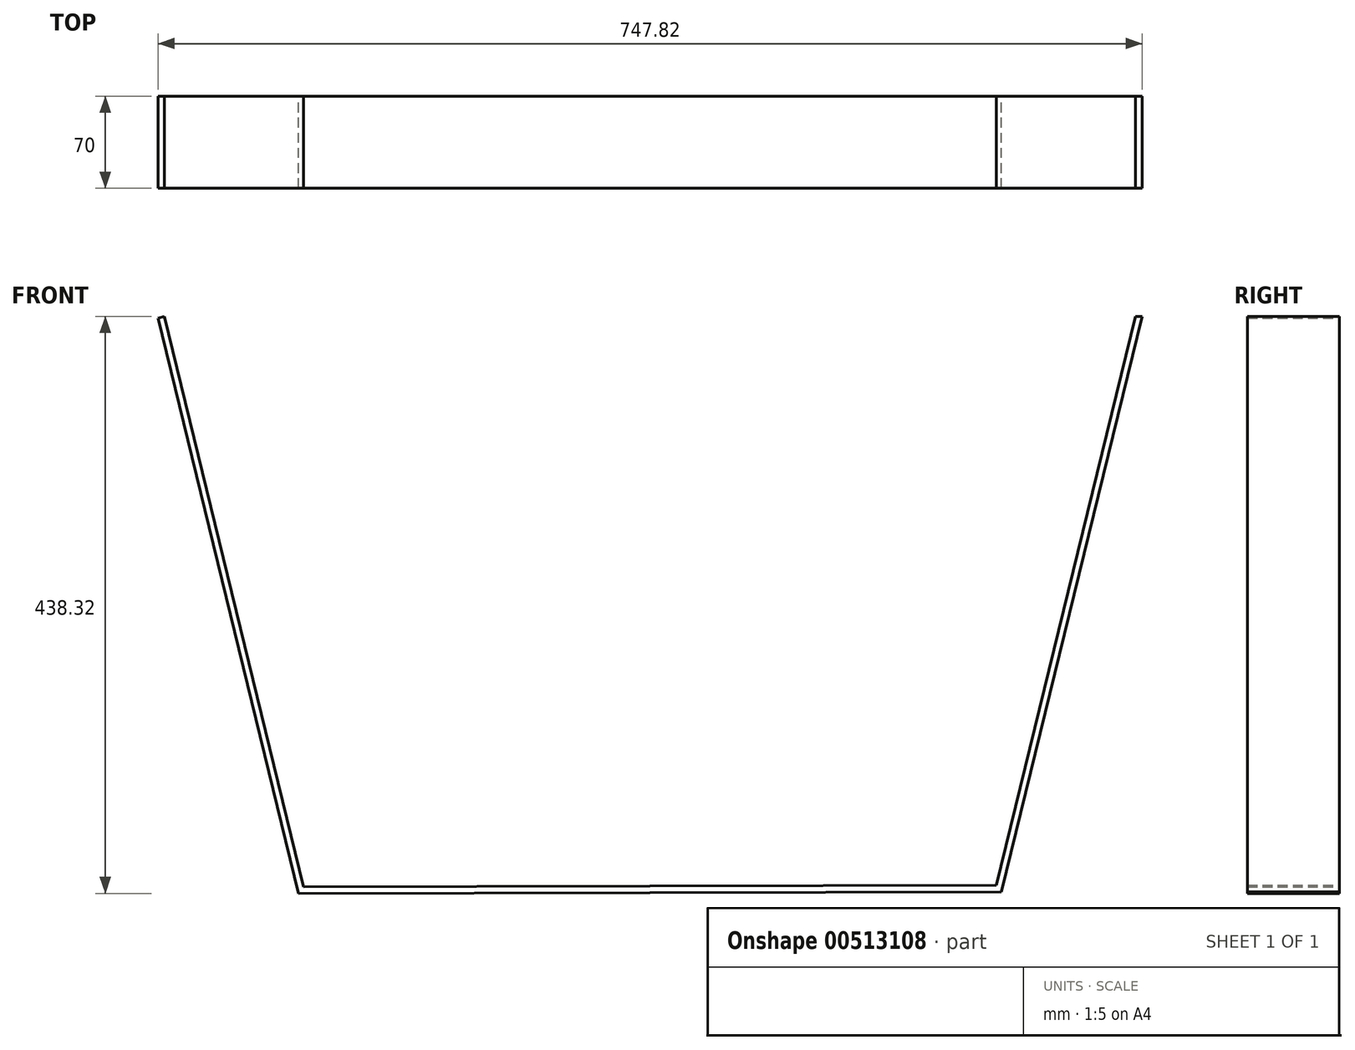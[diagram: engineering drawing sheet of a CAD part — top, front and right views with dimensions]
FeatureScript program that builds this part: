
annotation { "Feature Type Name" : "Feature", "Feature Type Description" : "" }
export const myFeature = defineFeature(function(context is Context, id is Id, definition is map)
    precondition{}
    {
        {
            var Q0;
            Q0=qCreatedBy(makeId("Front.planeOp"),FACE);
            var sketch = newSketch(context, id + "F0", { "sketchPlane" : qUnion([Q0])});
            skLineSegment(sketch, "E0.1", {"start": v(-436.34, 213.95) * mm, "end": v(-436.34, -176.05) * mm});
            skLineSegment(sketch, "E0.3", {"start": v(103.66, 213.95) * mm, "end": v(103.66, -176.05) * mm});
            skLineSegment(sketch, "E1", {"start": v(-465.58, -206.05) * mm, "end": v(133.66, -206.05) * mm});
            skLineSegment(sketch, "E2", {"start": v(-436.34, -176.05) * mm, "end": v(103.66, -176.05) * mm});
            skLineSegment(sketch, "E3", {"start": v(-436.34, 213.95) * mm, "end": v(103.66, 213.95) * mm});
            skLineSegment(sketch, "E4", {"start": v(-465.58, 243.95) * mm, "end": v(133.66, 243.95) * mm});
            skLineSegment(sketch, "E5", {"start": v(-465.58, 243.95) * mm, "end": v(-575.58, 243.95) * mm});
            skLineSegment(sketch, "E6", {"start": v(133.66, 243.95) * mm, "end": v(243.66, 243.95) * mm});
            skLineSegment(sketch, "E7", {"start": v(-575.58, 243.95) * mm, "end": v(-465.58, -206.05) * mm});
            skLineSegment(sketch, "E8", {"start": v(243.66, 243.95) * mm, "end": v(133.66, -206.05) * mm});
            skLineSegment(sketch, "E9.0", {"start": v(-537.36, 213.95) * mm, "end": v(-495.58, 43.02) * mm});
            skLineSegment(sketch, "E9.1", {"start": v(-495.58, 213.95) * mm, "end": v(-537.36, 213.95) * mm});
            skLineSegment(sketch, "E9.2", {"start": v(-495.58, 213.95) * mm, "end": v(-495.58, 43.02) * mm});
            skLineSegment(sketch, "E10.0", {"start": v(205.44, 213.95) * mm, "end": v(163.66, 43.02) * mm});
            skLineSegment(sketch, "E10.1", {"start": v(163.66, 213.95) * mm, "end": v(205.44, 213.95) * mm});
            skLineSegment(sketch, "E10.2", {"start": v(163.66, 213.95) * mm, "end": v(163.66, 43.02) * mm});
            skSolve(sketch);
        }
        {
            var Q0;
            Q0=makeQuery(id+"F0.imprint","IMPRINT",FACE,{"disambiguationData":[TD([[makeQuery(id+"F0.imprint","IMPRINT",EDGE,{"derivedFrom":sQuery(id+"F0.wireOp",EDGE,"E0.1")}),-1.0]])]});
            extrude(context, id + "F1", {"entities" : qUnion([Q0]), "depth" : 10 * mm, "offsetDistance" : 25 * mm});
        }
        {
            var Q0;
            Q0=makeQuery(id+"F3IlMBoAA892EVb_1.boolean.opBoolean","MERGE",FACE,{"derivedFrom":[makeQuery(id+"F1.opExtrude","CAP_FACE",FACE,{"disambiguationData":[OSD([sQuery(id+"F0.wireOp",EDGE,"E0.1"),sQuery(id+"F0.wireOp",EDGE,"E0.3"),sQuery(id+"F0.wireOp",EDGE,"E1"),sQuery(id+"F0.wireOp",EDGE,"E2"),sQuery(id+"F0.wireOp",EDGE,"E3"),sQuery(id+"F0.wireOp",EDGE,"E4"),sQuery(id+"F0.wireOp",EDGE,"E5"),sQuery(id+"F0.wireOp",EDGE,"E6"),sQuery(id+"F0.wireOp",EDGE,"E7"),sQuery(id+"F0.wireOp",EDGE,"E8"),sQuery(id+"F0.wireOp",EDGE,"E9.0"),sQuery(id+"F0.wireOp",EDGE,"E9.1"),sQuery(id+"F0.wireOp",EDGE,"E9.2"),sQuery(id+"F0.wireOp",EDGE,"E10.0"),sQuery(id+"F0.wireOp",EDGE,"E10.1"),sQuery(id+"F0.wireOp",EDGE,"E10.2")])],"isStart":false}),makeQuery(id+"F3IlMBoAA892EVb_1.opExtrude","CAP_FACE",FACE,{"disambiguationData":[OSD([sQuery(id+"FP2IF9D3UcjJ0pY_1.wireOp",EDGE,"tFwvSfep-dbMl-HYqX-lVeH-PwqNCjbaBwcB.bottom"),sQuery(id+"FP2IF9D3UcjJ0pY_1.wireOp",EDGE,"tFwvSfep-dbMl-HYqX-lVeH-PwqNCjbaBwcB.top"),sQuery(id+"FP2IF9D3UcjJ0pY_1.wireOp",EDGE,"tFwvSfep-dbMl-HYqX-lVeH-PwqNCjbaBwcB.left"),sQuery(id+"FP2IF9D3UcjJ0pY_1.wireOp",EDGE,"tFwvSfep-dbMl-HYqX-lVeH-PwqNCjbaBwcB.right"),sQuery(id+"FP2IF9D3UcjJ0pY_1.wireOp",EDGE,"Y96eg0lF-fkxR-g5Fa-GVY1-diRnflrGGg4P")])],"isStart":true}),makeQuery(id+"F3IlMBoAA892EVb_1.opExtrude","CAP_FACE",FACE,{"disambiguationData":[OSD([sQuery(id+"FP2IF9D3UcjJ0pY_1.wireOp",EDGE,"ks5o4KPP-mAZI-cY2u-NEqN-gQRgHeigmK98.bottom"),sQuery(id+"FP2IF9D3UcjJ0pY_1.wireOp",EDGE,"ks5o4KPP-mAZI-cY2u-NEqN-gQRgHeigmK98.top"),sQuery(id+"FP2IF9D3UcjJ0pY_1.wireOp",EDGE,"ks5o4KPP-mAZI-cY2u-NEqN-gQRgHeigmK98.left"),sQuery(id+"FP2IF9D3UcjJ0pY_1.wireOp",EDGE,"ks5o4KPP-mAZI-cY2u-NEqN-gQRgHeigmK98.right"),sQuery(id+"FP2IF9D3UcjJ0pY_1.wireOp",EDGE,"LuC45Tir-nWdd-Ql7E-cOUi-tOq3i7BzUPKw")])],"isStart":true}),makeQuery(id+"F3IlMBoAA892EVb_1.opExtrude","CAP_FACE",FACE,{"disambiguationData":[OSD([sQuery(id+"FP2IF9D3UcjJ0pY_1.wireOp",EDGE,"oF6x39j1-r8qr-EbSy-JxTa-gCMW2aaHiXhm.bottom"),sQuery(id+"FP2IF9D3UcjJ0pY_1.wireOp",EDGE,"oF6x39j1-r8qr-EbSy-JxTa-gCMW2aaHiXhm.top"),sQuery(id+"FP2IF9D3UcjJ0pY_1.wireOp",EDGE,"oF6x39j1-r8qr-EbSy-JxTa-gCMW2aaHiXhm.left"),sQuery(id+"FP2IF9D3UcjJ0pY_1.wireOp",EDGE,"oF6x39j1-r8qr-EbSy-JxTa-gCMW2aaHiXhm.right"),sQuery(id+"FP2IF9D3UcjJ0pY_1.wireOp",EDGE,"fuYv60Sf-LqG4-MogN-L5sv-ihyK4eeJ1hdm")])],"isStart":true}),makeQuery(id+"F3IlMBoAA892EVb_1.opExtrude","CAP_FACE",FACE,{"disambiguationData":[OSD([sQuery(id+"FP2IF9D3UcjJ0pY_1.wireOp",EDGE,"mDrYYbPc-NiZH-64na-iOjJ-N44UIPTyO1y5.bottom"),sQuery(id+"FP2IF9D3UcjJ0pY_1.wireOp",EDGE,"mDrYYbPc-NiZH-64na-iOjJ-N44UIPTyO1y5.top"),sQuery(id+"FP2IF9D3UcjJ0pY_1.wireOp",EDGE,"mDrYYbPc-NiZH-64na-iOjJ-N44UIPTyO1y5.left"),sQuery(id+"FP2IF9D3UcjJ0pY_1.wireOp",EDGE,"mDrYYbPc-NiZH-64na-iOjJ-N44UIPTyO1y5.right"),sQuery(id+"FP2IF9D3UcjJ0pY_1.wireOp",EDGE,"UzdDghzj-vJ60-MObE-3QK3-gFqXwsncNQI8")])],"isStart":true})]});
            var sketch = newSketch(context, id + "F2", { "sketchPlane" : qUnion([Q0])});
            skLineSegment(sketch, "E11", {"start": v(-575.58, 243.95) * mm, "end": v(-456.03, 243.95) * mm});
            skLineSegment(sketch, "E12", {"start": v(-575.58, 243.95) * mm, "end": v(-549.75, 138.3) * mm});
            skLineSegment(sketch, "E13", {"start": v(-465.58, -206.05) * mm, "end": v(-524.94, 36.8) * mm});
            skLineSegment(sketch, "E14", {"start": v(-524.94, 36.8) * mm, "end": v(193.02, 36.8) * mm});
            skLineSegment(sketch, "E15", {"start": v(193.02, 36.8) * mm, "end": v(133.66, -206.05) * mm});
            skLineSegment(sketch, "E16", {"start": v(-524.94, 36.8) * mm, "end": v(-534.94, 36.8) * mm});
            skLineSegment(sketch, "E17", {"start": v(193.02, 36.8) * mm, "end": v(203.02, 36.8) * mm});
            skLineSegment(sketch, "E18", {"start": v(-534.94, 36.8) * mm, "end": v(-475.58, -206.05) * mm});
            skLineSegment(sketch, "E19", {"start": v(203.02, 36.8) * mm, "end": v(143.25, -207.72) * mm});
            skLineSegment(sketch, "E20", {"start": v(-534.94, 36.8) * mm, "end": v(-539.8, 35.6) * mm});
            skLineSegment(sketch, "E21", {"start": v(-539.8, 35.6) * mm, "end": v(-432.95, -401.52) * mm});
            skLineSegment(sketch, "E22", {"start": v(203.02, 36.8) * mm, "end": v(208.02, 36.8) * mm});
            skLineSegment(sketch, "E23", {"start": v(208.02, 36.8) * mm, "end": v(101.17, -400.33) * mm});
            skLineSegment(sketch, "E24", {"start": v(-432.95, -401.52) * mm, "end": v(101.17, -400.33) * mm});
            skLineSegment(sketch, "E25.0", {"start": v(203.17, 37.98) * mm, "end": v(97.24, -395.34) * mm});
            skLineSegment(sketch, "E25.1", {"start": v(-429.02, -396.51) * mm, "end": v(97.24, -395.34) * mm});
            skLineSegment(sketch, "E25.2", {"start": v(-534.94, 36.8) * mm, "end": v(-429.02, -396.51) * mm});
            skSolve(sketch);
        }
        {
            var Q0;
            {var subQ1=sQuery(id+"F2.wireOp",EDGE,"E20");Q0=makeQuery(id+"F2.imprint","IMPRINT",FACE,{"disambiguationData":[TD([[makeQuery(id+"F2.imprint","IMPRINT",EDGE,{"derivedFrom":subQ1}),1.0]])]});}
            extrude(context, id + "F3", {"entities" : qUnion([Q0]), "depth" : 70 * mm, "offsetDistance" : 25 * mm});
        }
        {
            var Q0;
            Q0=makeQuery(id+"F1.opExtrude","CAP_FACE",FACE,{"disambiguationData":[OSD([sQuery(id+"F0.wireOp",EDGE,"E0.1"),sQuery(id+"F0.wireOp",EDGE,"E0.3"),sQuery(id+"F0.wireOp",EDGE,"E1"),sQuery(id+"F0.wireOp",EDGE,"E2"),sQuery(id+"F0.wireOp",EDGE,"E3"),sQuery(id+"F0.wireOp",EDGE,"E4"),sQuery(id+"F0.wireOp",EDGE,"E5"),sQuery(id+"F0.wireOp",EDGE,"E6"),sQuery(id+"F0.wireOp",EDGE,"E7"),sQuery(id+"F0.wireOp",EDGE,"E8"),sQuery(id+"F0.wireOp",EDGE,"E9.0"),sQuery(id+"F0.wireOp",EDGE,"E9.1"),sQuery(id+"F0.wireOp",EDGE,"E9.2"),sQuery(id+"F0.wireOp",EDGE,"E10.0"),sQuery(id+"F0.wireOp",EDGE,"E10.1"),sQuery(id+"F0.wireOp",EDGE,"E10.2")])],"isStart":false});
            extrude(context, id + "F4", {"entities" : qUnion([Q0]), "operationType" : NewBodyOperationType.REMOVE, "oppositeDirection" : true, "depth" : 25 * mm, "offsetDistance" : 25 * mm});
        }
    });
